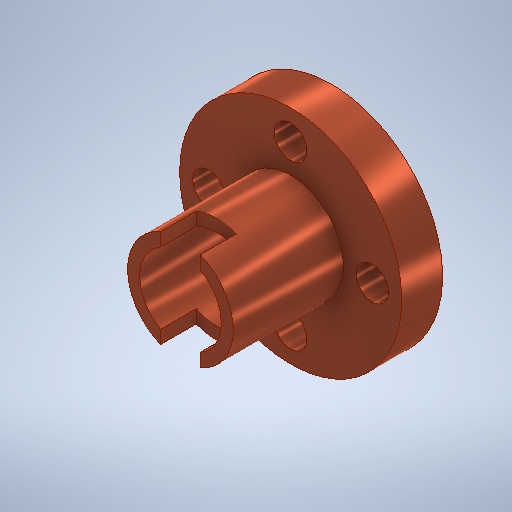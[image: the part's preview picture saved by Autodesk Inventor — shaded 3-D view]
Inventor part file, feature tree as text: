
AUTODESK INVENTOR PART (.ipt)
format: ipt  version: 2025.2 (Build 292293000, 293)  size: 305,152 bytes
history: native  units: mm
features: sketch x6, extrude x3, other x1, hole x1, projected_geometry x1
ambient origin geometry x8: Origin, YZ Plane, XZ Plane, XY Plane, X Axis, Y Axis, Z Axis, Center Point
bodies: Body1 (feature_tree)
feature tree (12):
  other  "Bryła1"
  extrude  "Wyciągnięcie proste1"  Depth=8.0mm
  hole  "Otwór1"  [1 undecoded]
  extrude  "Wyciągnięcie proste2"  Depth=4.0mm TaperAngle=0.0deg
  extrude  "Wyciągnięcie proste3"  Depth=3.9mm TaperAngle=360.0deg
  sketch  "Szkic1"
  sketch  "Sketch Circular Pattern1"  dims[d0=21.75mm d1=8.0mm]
  sketch  "Szkic2"
  projected_geometry  "Pętla rzutowana1"
  sketch  "Sketch Circular Pattern2"  dims[d2=8.0mm d3=40.0mm d5=360.0deg d7=4.0mm d8=0.0mm d9=40.0mm d11=360.0deg d13=3.2mm d14=6.0mm d15=4.0mm d16=2.0mm d17=90.0deg d18=8.0mm d19=20.594885mm d20=8.0mm d21=10.34mm d22=10.8mm d23=0.0mm d24=10.34mm d25=7.3mm d26=10.34mm d27=3.9mm d28=0.0mm]
  sketch  "Szkic3"
  sketch  "Szkic4"
note: 1 required parameter value undecoded (feature->parameter linkage not recoverable at this tier; creation-order binding heuristic only, values carry confidence <= 0.55)
